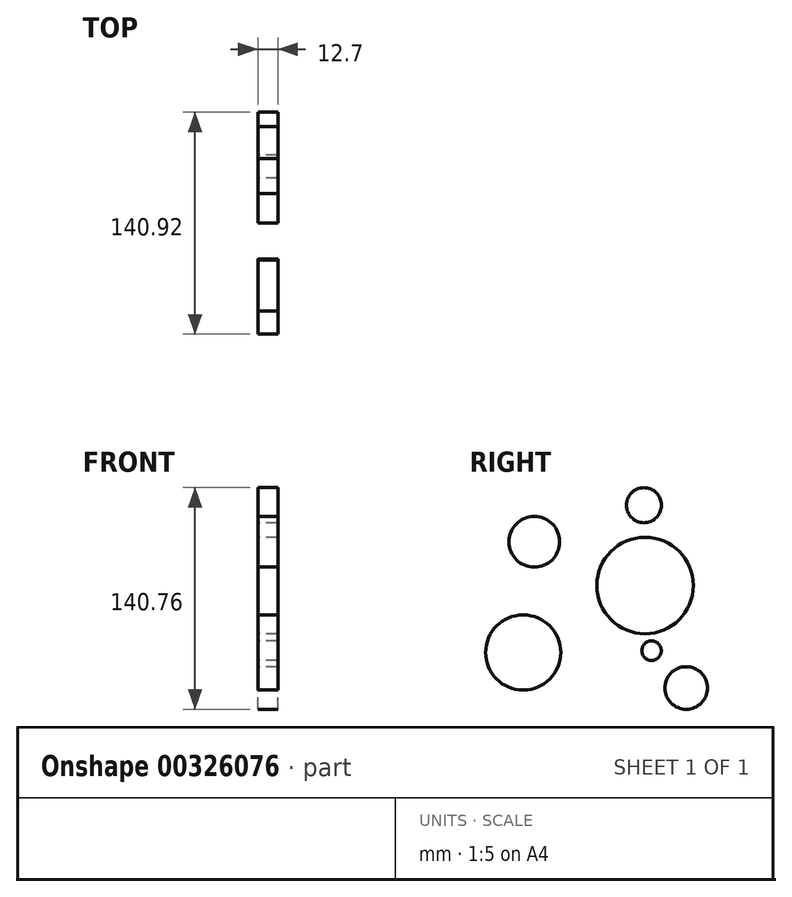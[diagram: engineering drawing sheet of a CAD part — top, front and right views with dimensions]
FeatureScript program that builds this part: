
annotation { "Feature Type Name" : "Feature", "Feature Type Description" : "" }
export const myFeature = defineFeature(function(context is Context, id is Id, definition is map)
    precondition{}
    {
        {
            var Q0;
            Q0=qCreatedBy(makeId("Right.planeOp"),FACE);
            var sketch = newSketch(context, id + "F0", { "sketchPlane" : qUnion([Q0])});
            skCircle(sketch, "E0", {"center": v(61.43, -65.1) * mm, "radius": 13.52 * mm});
            skCircle(sketch, "E1", {"center": v(39.45, -41.4) * mm, "radius": 6.18 * mm});
            skCircle(sketch, "E2", {"center": v(35.35, 0) * mm, "radius": 30.65 * mm});
            skCircle(sketch, "E3", {"center": v(-35.03, 27.75) * mm, "radius": 16.1 * mm});
            skCircle(sketch, "E4", {"center": v(-42.1, -42.6) * mm, "radius": 23.86 * mm});
            skCircle(sketch, "E5", {"center": v(34.58, 51) * mm, "radius": 11.14 * mm});
            skSolve(sketch);
        }
        {
            var Q0;
            Q0 = qSketchRegion(id + "F0", true);
            extrude(context, id + "F1", {"entities" : qUnion([Q0]), "depth" : 12.7 * mm});
        }
    });
